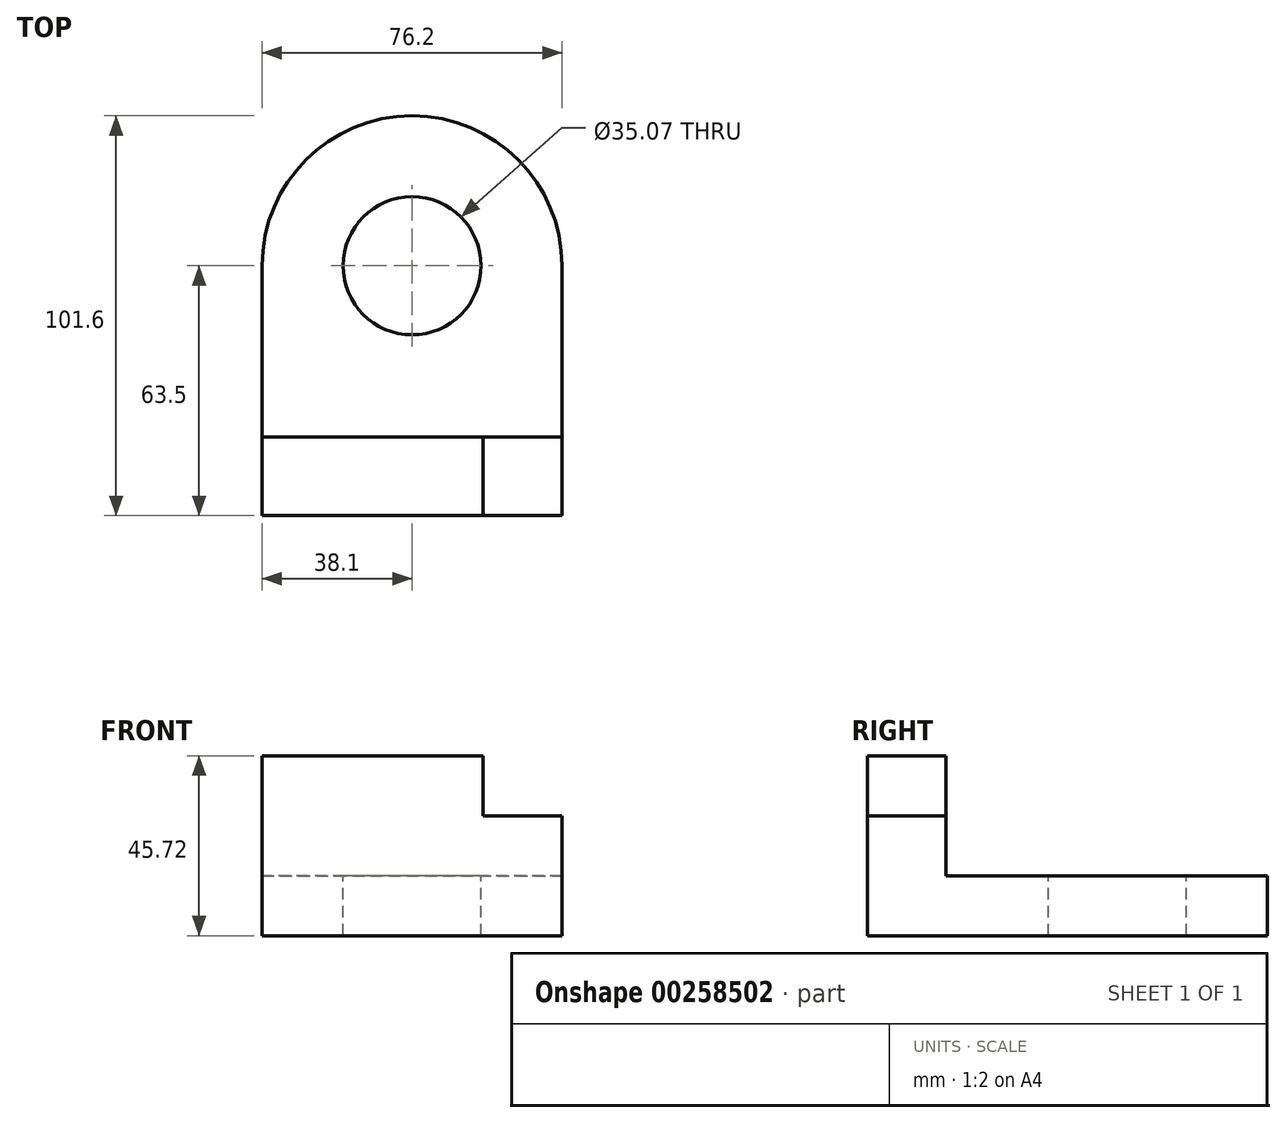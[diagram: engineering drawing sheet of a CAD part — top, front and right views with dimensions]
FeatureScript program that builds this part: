
annotation { "Feature Type Name" : "Feature", "Feature Type Description" : "" }
export const myFeature = defineFeature(function(context is Context, id is Id, definition is map)
    precondition{}
    {
        {
            var Q0;
            Q0=qCreatedBy(makeId("Top.planeOp"),FACE);
            var sketch = newSketch(context, id + "F0", { "sketchPlane" : qUnion([Q0])});
            skLineSegment(sketch, "E0.bottom", {"start": v(38.1, -31.75) * mm, "end": v(-38.1, -31.75) * mm});
            skLineSegment(sketch, "E0.top", {"start": v(38.1, 31.75) * mm, "end": v(-38.1, 31.75) * mm});
            skLineSegment(sketch, "E0.left", {"start": v(38.1, -31.75) * mm, "end": v(38.1, 31.75) * mm});
            skLineSegment(sketch, "E0.right", {"start": v(-38.1, -31.75) * mm, "end": v(-38.1, 31.75) * mm});
            skPoint(sketch, "E0.middle", {"position": v(0, 0) * mm});
            skArc(sketch, "E1", {"start": v(-38.1, 31.75) * mm, "mid": v(0, 69.85) * mm, "end": v(38.1, 31.75) * mm});
            skSolve(sketch);
        }
        {
            var Q0;
            Q0=makeQuery(id+"F0.imprint","IMPRINT",FACE,{"disambiguationData":[TD([[makeQuery(id+"F0.imprint","IMPRINT",EDGE,{"derivedFrom":sQuery(id+"F0.wireOp",EDGE,"E0.top")}),-1.0]])]});
            var Q1;
            Q1=makeQuery(id+"F0.imprint","IMPRINT",FACE,{"disambiguationData":[TD([[makeQuery(id+"F0.imprint","IMPRINT",EDGE,{"derivedFrom":sQuery(id+"F0.wireOp",EDGE,"E0.bottom")}),-1.0]])]});
            extrude(context, id + "F1", {"entities" : qUnion([Q0, Q1]), "depth" : 15.24 * mm});
        }
        {
            var Q0;
            Q0=makeQuery(id+"F1.opExtrude","CAP_FACE",FACE,{"disambiguationData":[OSD([sQuery(id+"F0.wireOp",EDGE,"E0.bottom"),sQuery(id+"F0.wireOp",EDGE,"E0.left"),sQuery(id+"F0.wireOp",EDGE,"E0.right"),sQuery(id+"F0.wireOp",EDGE,"E1")])],"isStart":false});
            var sketch = newSketch(context, id + "F2", { "sketchPlane" : qUnion([Q0])});
            skCircle(sketch, "E2", {"center": v(0, 31.75) * mm, "radius": 17.54 * mm});
            skSolve(sketch);
        }
        {
            var Q0;
            Q0=makeQuery(id+"F2.imprint","IMPRINT",FACE,{"disambiguationData":[TD([[makeQuery(id+"F2.imprint","IMPRINT",EDGE,{"derivedFrom":sQuery(id+"F2.wireOp",EDGE,"E2")}),1.0]])]});
            extrude(context, id + "F3", {"entities" : qUnion([Q0]), "operationType" : NewBodyOperationType.REMOVE, "endBound" : BoundingType.THROUGH_ALL, "oppositeDirection" : true, "depth" : 25.4 * mm});
        }
        {
            var Q0;
            Q0=makeQuery(id+"F1.opExtrude","CAP_FACE",FACE,{"disambiguationData":[OSD([sQuery(id+"F0.wireOp",EDGE,"E0.bottom"),sQuery(id+"F0.wireOp",EDGE,"E0.left"),sQuery(id+"F0.wireOp",EDGE,"E0.right"),sQuery(id+"F0.wireOp",EDGE,"E1")])],"isStart":false});
            var sketch = newSketch(context, id + "F4", { "sketchPlane" : qUnion([Q0])});
            skLineSegment(sketch, "E3.bottom", {"start": v(-38.1, -11.74) * mm, "end": v(38.1, -11.74) * mm});
            skLineSegment(sketch, "E3.top", {"start": v(-38.1, -31.75) * mm, "end": v(38.1, -31.75) * mm});
            skLineSegment(sketch, "E3.left", {"start": v(-38.1, -11.74) * mm, "end": v(-38.1, -31.75) * mm});
            skLineSegment(sketch, "E3.right", {"start": v(38.1, -11.74) * mm, "end": v(38.1, -31.75) * mm});
            skSolve(sketch);
        }
        {
            var Q0;
            Q0=makeQuery(id+"F4.imprint","IMPRINT",FACE,{"disambiguationData":[TD([[makeQuery(id+"F4.imprint","IMPRINT",EDGE,{"derivedFrom":sQuery(id+"F4.wireOp",EDGE,"E3.bottom")}),-1.0]])]});
            extrude(context, id + "F5", {"entities" : qUnion([Q0]), "operationType" : NewBodyOperationType.ADD, "depth" : 30.48 * mm});
        }
        {
            var Q0;
            Q0=makeQuery(id+"F5.opExtrude","CAP_FACE",FACE,{"disambiguationData":[OSD([sQuery(id+"F4.wireOp",EDGE,"E3.bottom"),sQuery(id+"F4.wireOp",EDGE,"E3.top"),sQuery(id+"F4.wireOp",EDGE,"E3.left"),sQuery(id+"F4.wireOp",EDGE,"E3.right")])],"isStart":false});
            var sketch = newSketch(context, id + "F6", { "sketchPlane" : qUnion([Q0])});
            skLineSegment(sketch, "E4.bottom", {"start": v(38.1, -31.75) * mm, "end": v(18.08, -31.75) * mm});
            skLineSegment(sketch, "E4.top", {"start": v(38.1, -11.74) * mm, "end": v(18.08, -11.74) * mm});
            skLineSegment(sketch, "E4.left", {"start": v(38.1, -31.75) * mm, "end": v(38.1, -11.74) * mm});
            skLineSegment(sketch, "E4.right", {"start": v(18.08, -31.75) * mm, "end": v(18.08, -11.74) * mm});
            skSolve(sketch);
        }
        {
            var Q0;
            Q0=makeQuery(id+"F6.imprint","IMPRINT",FACE,{"disambiguationData":[TD([[makeQuery(id+"F6.imprint","IMPRINT",EDGE,{"derivedFrom":sQuery(id+"F6.wireOp",EDGE,"E4.bottom")}),-1.0]])]});
            extrude(context, id + "F7", {"entities" : qUnion([Q0]), "operationType" : NewBodyOperationType.REMOVE, "oppositeDirection" : true, "depth" : 15.24 * mm});
        }
    });
